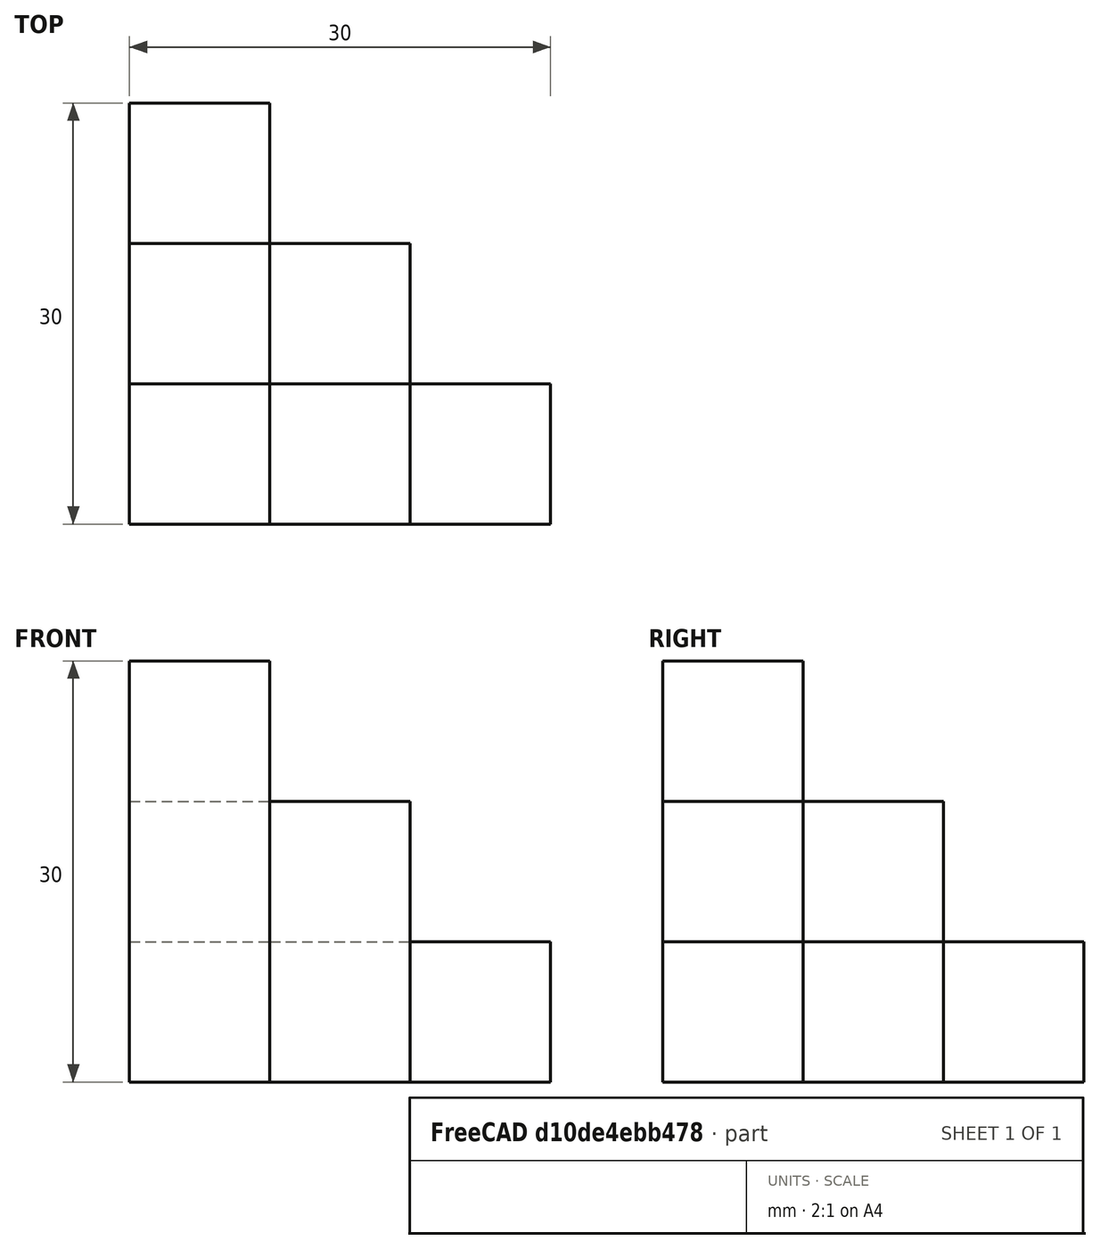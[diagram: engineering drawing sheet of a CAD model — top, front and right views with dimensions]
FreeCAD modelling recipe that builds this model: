
FCSTD DOCUMENT  (FreeCAD 1.0R39319 (Git))
Label: ojt_t04r01_qbert3levels
License: All rights reserved
LicenseURL: https://en.wikipedia.org/wiki/All_rights_reserved
objects: Part::Box×6
note: 6 computed .brp shape members not serialized (recipe doc carries the construction recipe); baked Part::Feature solids carry a one-line shape summary decoded from their .brp

FEATURE [Part::Box] Box  label="nivel1-micubo-1"
  AttacherType = Attacher::AttachEngine3D
  Height = 30
  Length = 10
  Width = 10
FEATURE [Part::Box] Box001  label="nivel2-micubillo-1"
  AttacherType = Attacher::AttachEngine3D
  Height = 20
  Length = 10
  Placement = pos=(10,0,0) rot=(0,0,1;0rad)
  Width = 10
FEATURE [Part::Box] Box002  label="nivel2-micubon-2"
  AttacherType = Attacher::AttachEngine3D
  Height = 20
  Length = 10
  Placement = pos=(0,10,0) rot=(0,0,1;0rad)
  Width = 10
FEATURE [Part::Box] Box003  label="Cub"
  AttacherType = Attacher::AttachEngine3D
  Height = 10
  Length = 10
  Placement = pos=(20,0,0) rot=(0,0,1;0rad)
  Width = 10
FEATURE [Part::Box] Box004  label="Cub001"
  AttacherType = Attacher::AttachEngine3D
  Height = 10
  Length = 10
  Placement = pos=(0,20,0) rot=(0,0,1;0rad)
  Width = 10
FEATURE [Part::Box] Box005  label="Cub002"
  AttacherType = Attacher::AttachEngine3D
  Height = 10
  Length = 10
  Placement = pos=(10,10,0) rot=(0,0,1;0rad)
  Width = 10
